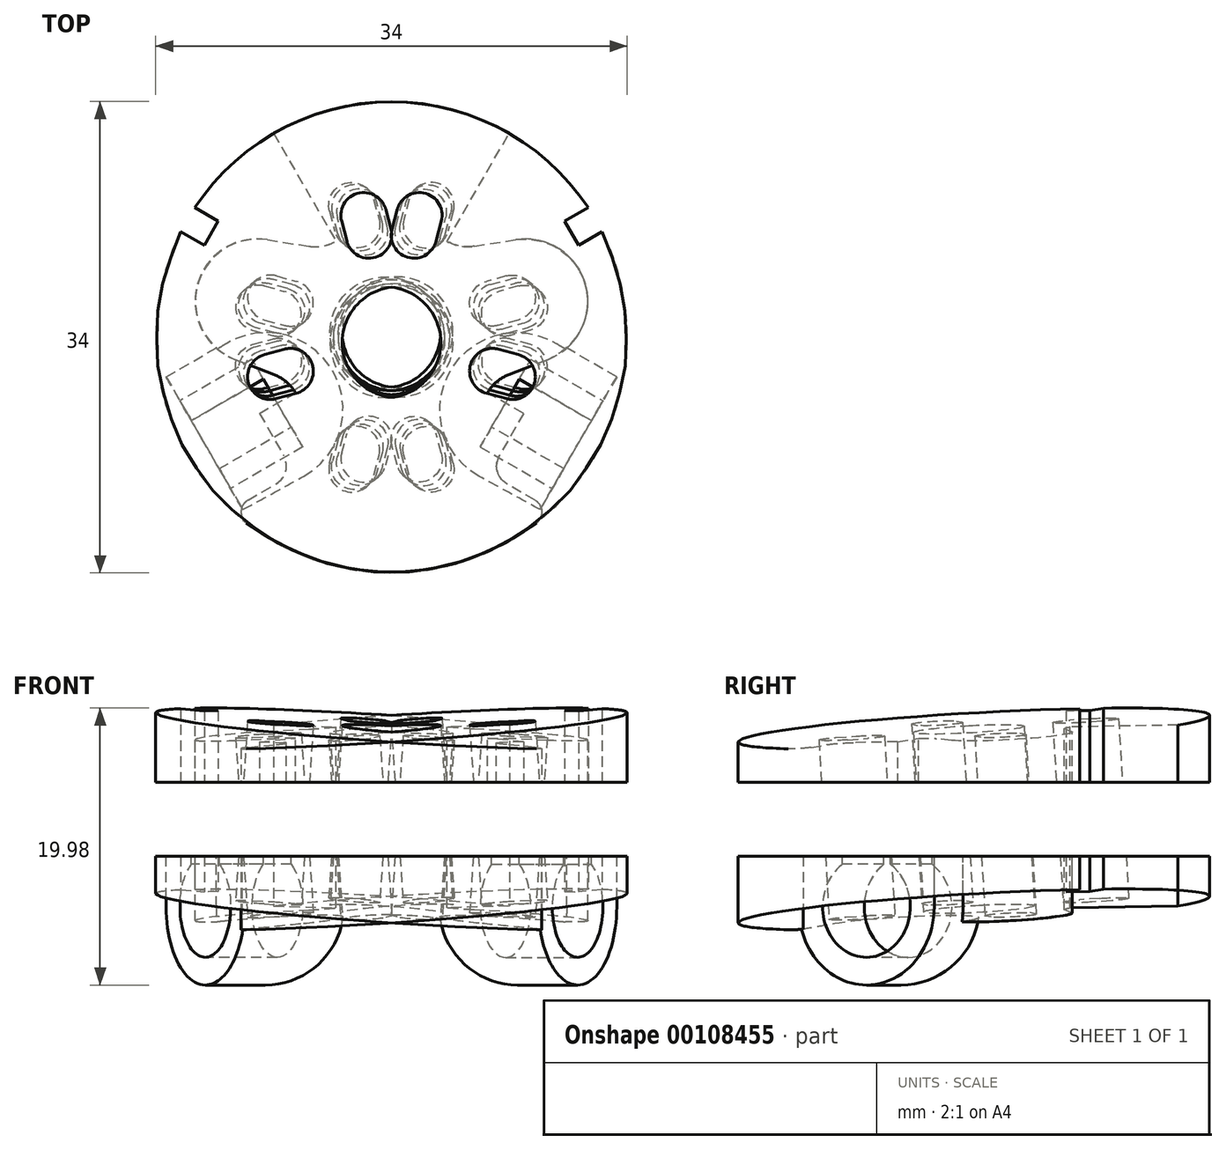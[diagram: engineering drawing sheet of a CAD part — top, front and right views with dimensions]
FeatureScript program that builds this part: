
annotation { "Feature Type Name" : "Feature", "Feature Type Description" : "" }
export const myFeature = defineFeature(function(context is Context, id is Id, definition is map)
    precondition{}
    {
        {
            var Q0;
            Q0=qCreatedBy(makeId("Top.planeOp"),FACE);
            var sketch = newSketch(context, id + "F0", { "sketchPlane" : qUnion([Q0])});
            skCircle(sketch, "E0", {"center": v(0, 0) * mm, "radius": 17 * mm});
            skLineSegment(sketch, "E1", {"start": v(10.93, 13.02) * mm, "end": v(-10.93, -13.02) * mm, "construction": true});
            skLineSegment(sketch, "E2", {"start": v(-8.5, -14.72) * mm, "end": v(8.5, 14.72) * mm, "construction": true});
            skSolve(sketch);
        }
        {
            var Q0;
            Q0=qCreatedBy(makeId("Top.planeOp"),FACE);
            var sketch = newSketch(context, id + "F1", { "sketchPlane" : qUnion([Q0])});
            skLineSegment(sketch, "E3", {"start": v(-8.5, -14.72) * mm, "end": v(8.5, 14.72) * mm, "construction": true});
            skPoint(sketch, "E4", {"position": v(0, 0) * mm});
            skLineSegment(sketch, "E5", {"start": v(0, 0) * mm, "end": v(9.18, 2.46) * mm, "construction": true});
            skPoint(sketch, "E6", {"position": v(7.73, 2.07) * mm});
            skArc(sketch, "E7", {"start": v(9.6, 0.91) * mm, "mid": v(10.72, 2.87) * mm, "end": v(8.76, 4) * mm, "construction": true});
            skArc(sketch, "E8", {"start": v(7.31, 3.62) * mm, "mid": v(6.18, 1.66) * mm, "end": v(8.14, 0.53) * mm, "construction": true});
            skLineSegment(sketch, "E9", {"start": v(8.76, 4) * mm, "end": v(7.31, 3.62) * mm, "construction": true});
            skLineSegment(sketch, "E10", {"start": v(9.6, 0.91) * mm, "end": v(8.14, 0.53) * mm, "construction": true});
            skLineSegment(sketch, "E11.1.0", {"start": v(-4, 8.76) * mm, "end": v(-3.62, 7.31) * mm, "construction": true});
            skLineSegment(sketch, "E11.1.1", {"start": v(-0.91, 9.6) * mm, "end": v(-0.53, 8.14) * mm, "construction": true});
            skArc(sketch, "E11.1.2", {"start": v(-3.62, 7.31) * mm, "mid": v(-1.66, 6.18) * mm, "end": v(-0.53, 8.14) * mm, "construction": true});
            skArc(sketch, "E11.1.3", {"start": v(-0.91, 9.6) * mm, "mid": v(-2.87, 10.72) * mm, "end": v(-4, 8.76) * mm, "construction": true});
            skPoint(sketch, "E11.1.4", {"position": v(-2.07, 7.73) * mm});
            skLineSegment(sketch, "E11.2.0", {"start": v(-8.76, -4) * mm, "end": v(-7.31, -3.62) * mm, "construction": true});
            skLineSegment(sketch, "E11.2.1", {"start": v(-9.6, -0.91) * mm, "end": v(-8.14, -0.53) * mm, "construction": true});
            skArc(sketch, "E11.2.2", {"start": v(-7.31, -3.62) * mm, "mid": v(-6.18, -1.66) * mm, "end": v(-8.14, -0.53) * mm, "construction": true});
            skArc(sketch, "E11.2.3", {"start": v(-9.6, -0.91) * mm, "mid": v(-10.72, -2.87) * mm, "end": v(-8.76, -4) * mm, "construction": true});
            skPoint(sketch, "E11.2.4", {"position": v(-7.73, -2.07) * mm});
            skLineSegment(sketch, "E11.3.0", {"start": v(4, -8.76) * mm, "end": v(3.62, -7.31) * mm, "construction": true});
            skLineSegment(sketch, "E11.3.1", {"start": v(0.91, -9.6) * mm, "end": v(0.53, -8.14) * mm, "construction": true});
            skArc(sketch, "E11.3.2", {"start": v(3.62, -7.31) * mm, "mid": v(1.66, -6.18) * mm, "end": v(0.53, -8.14) * mm, "construction": true});
            skArc(sketch, "E11.3.3", {"start": v(0.91, -9.6) * mm, "mid": v(2.87, -10.72) * mm, "end": v(4, -8.76) * mm, "construction": true});
            skPoint(sketch, "E11.3.4", {"position": v(2.07, -7.73) * mm});
            skSolve(sketch);
        }
        {
            var Q0;
            Q0=sQuery(id+"F0.wireOp",EDGE,"E1");
            cPlane(context, id + "F2", {"entities" : qUnion([Q0]), "cplaneType" : CPlaneType.LINE_ANGLE, "offset" : 25 * mm, "angle" : 355 * degree, "width" : 150 * mm, "height" : 150 * mm});
        }
        {
            var Q0;
            Q0=qCreatedBy(id+"F2.planeOp",FACE);
            var sketch = newSketch(context, id + "F3", { "sketchPlane" : qUnion([Q0])});
            skLineSegment(sketch, "E12", {"start": v(0, 0) * mm, "end": v(9.18, -2.44) * mm, "construction": true});
            skPoint(sketch, "E13", {"position": v(7.73, -2.06) * mm});
            skArc(sketch, "E14", {"start": v(8.76, -4.04) * mm, "mid": v(10.78, -2.87) * mm, "end": v(9.6, -0.85) * mm});
            skArc(sketch, "E15", {"start": v(8.16, -0.46) * mm, "mid": v(6.14, -1.63) * mm, "end": v(7.3, -3.65) * mm});
            skLineSegment(sketch, "E16", {"start": v(7.3, -3.65) * mm, "end": v(8.76, -4.04) * mm});
            skLineSegment(sketch, "E17", {"start": v(8.16, -0.46) * mm, "end": v(9.6, -0.85) * mm});
            skCircle(sketch, "E18", {"center": v(0, 0) * mm, "radius": 4 * mm});
            skLineSegment(sketch, "E19.1.0", {"start": v(0.46, 8.16) * mm, "end": v(0.85, 9.6) * mm});
            skLineSegment(sketch, "E19.1.1", {"start": v(3.65, 7.31) * mm, "end": v(4.04, 8.76) * mm});
            skArc(sketch, "E19.1.2", {"start": v(0.46, 8.16) * mm, "mid": v(1.63, 6.14) * mm, "end": v(3.65, 7.31) * mm});
            skArc(sketch, "E19.1.3", {"start": v(4.04, 8.76) * mm, "mid": v(2.87, 10.78) * mm, "end": v(0.85, 9.6) * mm});
            skPoint(sketch, "E19.1.4", {"position": v(2.06, 7.73) * mm});
            skLineSegment(sketch, "E19.2.0", {"start": v(-8.16, 0.47) * mm, "end": v(-9.6, 0.85) * mm});
            skLineSegment(sketch, "E19.2.1", {"start": v(-7.3, 3.66) * mm, "end": v(-8.76, 4.04) * mm});
            skArc(sketch, "E19.2.2", {"start": v(-8.16, 0.47) * mm, "mid": v(-6.14, 1.64) * mm, "end": v(-7.3, 3.66) * mm});
            skArc(sketch, "E19.2.3", {"start": v(-8.76, 4.04) * mm, "mid": v(-10.78, 2.87) * mm, "end": v(-9.6, 0.85) * mm});
            skPoint(sketch, "E19.2.4", {"position": v(-7.73, 2.06) * mm});
            skLineSegment(sketch, "E19.3.0", {"start": v(-0.47, -8.15) * mm, "end": v(-0.85, -9.6) * mm});
            skLineSegment(sketch, "E19.3.1", {"start": v(-3.65, -7.3) * mm, "end": v(-4.04, -8.76) * mm});
            skArc(sketch, "E19.3.2", {"start": v(-0.47, -8.15) * mm, "mid": v(-1.64, -6.14) * mm, "end": v(-3.65, -7.3) * mm});
            skArc(sketch, "E19.3.3", {"start": v(-4.04, -8.76) * mm, "mid": v(-2.87, -10.77) * mm, "end": v(-0.85, -9.6) * mm});
            skPoint(sketch, "E19.3.4", {"position": v(-2.06, -7.73) * mm});
            skSolve(sketch);
        }
        {
            var Q0;
            Q0=qSketchRegion(id+"F0",true);
            extrude(context, id + "F4", {"entities" : qUnion([Q0]), "endBound" : BoundingType.SYMMETRIC, "depth" : 25 * mm});
        }
        {
            var Q0;
            Q0=qSketchRegion(id+"F3",true);
            extrude(context, id + "F5", {"entities" : qUnion([Q0]), "operationType" : NewBodyOperationType.REMOVE, "endBound" : BoundingType.THROUGH_ALL, "oppositeDirection" : true, "depth" : 25 * mm, "hasSecondDirection" : true, "secondDirectionBound" : SecondDirectionBoundingType.THROUGH_ALL, "secondDirectionOppositeDirection" : false, "secondDirectionDepth" : 25 * mm});
        }
        {
            var Q0;
            Q0=qCreatedBy(id+"F2.planeOp",FACE);
            cPlane(context, id + "F6", {"entities" : qUnion([Q0]), "cplaneType" : CPlaneType.OFFSET, "offset" : 6.5 * mm, "oppositeDirection" : true, "width" : 150 * mm, "height" : 150 * mm});
        }
        {
            var Q0;
            Q0=qCreatedBy(id+"F2.planeOp",FACE);
            cPlane(context, id + "F7", {"entities" : qUnion([Q0]), "cplaneType" : CPlaneType.OFFSET, "offset" : 6.5 * mm, "width" : 150 * mm, "height" : 150 * mm});
        }
        {
            var Q0;
            Q0=qCreatedBy(id+"F6.planeOp",FACE);
            var sketch = newSketch(context, id + "F8", { "sketchPlane" : qUnion([Q0])});
            skCircle(sketch, "E20", {"center": v(0, 0) * mm, "radius": 20 * mm});
            skSolve(sketch);
        }
        {
            var Q0;
            Q0=qSketchRegion(id+"F8",true);
            var Q1;
            Q1=makeQuery(id+"F4.opExtrude","CAP_FACE",FACE,{"disambiguationData":[OSD([sQuery(id+"F0.wireOp",EDGE,"E0")])],"isStart":false});
            extrude(context, id + "F9", {"entities" : qUnion([Q0]), "operationType" : NewBodyOperationType.REMOVE, "endBound" : BoundingType.UP_TO_SURFACE, "oppositeDirection" : true, "endBoundEntityFace" : qUnion([Q1]), "depth" : 25 * mm});
        }
        {
            var Q0;
            Q0=qCreatedBy(id+"F7.planeOp",FACE);
            var sketch = newSketch(context, id + "F10", { "sketchPlane" : qUnion([Q0])});
            skCircle(sketch, "E21", {"center": v(0, 0) * mm, "radius": 20 * mm});
            skSolve(sketch);
        }
        {
            var Q0;
            Q0=qSketchRegion(id+"F10",true);
            var Q1;
            Q1=makeQuery(id+"F4.opExtrude","CAP_FACE",FACE,{"disambiguationData":[OSD([sQuery(id+"F0.wireOp",EDGE,"E0")])],"isStart":true});
            extrude(context, id + "F11", {"entities" : qUnion([Q0]), "operationType" : NewBodyOperationType.REMOVE, "endBound" : BoundingType.UP_TO_SURFACE, "endBoundEntityFace" : qUnion([Q1]), "depth" : 25 * mm});
        }
        {
            var Q0;
            Q0=qCreatedBy(makeId("Front.planeOp"),FACE);
            var sketch = newSketch(context, id + "F12", { "sketchPlane" : qUnion([Q0])});
            skLineSegment(sketch, "E22.bottom", {"start": v(20, 2.67) * mm, "end": v(-20, 2.67) * mm});
            skLineSegment(sketch, "E22.top", {"start": v(20, -2.67) * mm, "end": v(-20, -2.67) * mm});
            skLineSegment(sketch, "E22.left", {"start": v(20, 2.67) * mm, "end": v(20, -2.67) * mm});
            skLineSegment(sketch, "E22.right", {"start": v(-20, 2.67) * mm, "end": v(-20, -2.67) * mm});
            skPoint(sketch, "E22.middle", {"position": v(0, 0) * mm});
            skSolve(sketch);
        }
        {
            var Q0;
            Q0=qSketchRegion(id+"F12",true);
            extrude(context, id + "F13", {"entities" : qUnion([Q0]), "operationType" : NewBodyOperationType.REMOVE, "endBound" : BoundingType.THROUGH_ALL, "oppositeDirection" : true, "depth" : 25 * mm, "hasSecondDirection" : true, "secondDirectionBound" : SecondDirectionBoundingType.THROUGH_ALL, "secondDirectionOppositeDirection" : false, "secondDirectionDepth" : 25 * mm});
        }
        {
            var Q0;
            Q0=sQuery(id+"F1.wireOp",EDGE,"E3");
            cPlane(context, id + "F14", {"entities" : qUnion([Q0]), "cplaneType" : CPlaneType.LINE_ANGLE, "offset" : 25 * mm, "angle" : 90 * degree, "width" : 150 * mm, "height" : 150 * mm});
        }
        {
            var Q0;
            Q0=qCreatedBy(id+"F14.planeOp",FACE);
            cPlane(context, id + "F15", {"entities" : qUnion([Q0]), "cplaneType" : CPlaneType.OFFSET, "offset" : 17 * mm, "width" : 150 * mm, "height" : 150 * mm});
        }
        {
            var Q0;
            Q0=qCreatedBy(id+"F14.planeOp",FACE);
            cPlane(context, id + "F16", {"entities" : qUnion([Q0]), "cplaneType" : CPlaneType.OFFSET, "offset" : 17 * mm, "oppositeDirection" : true, "width" : 150 * mm, "height" : 150 * mm});
        }
        {
            var Q0;
            Q0=qCreatedBy(id+"F15.planeOp",FACE);
            var sketch = newSketch(context, id + "F17", { "sketchPlane" : qUnion([Q0])});
            skLineSegment(sketch, "E23.bottom", {"start": v(1, 12.5) * mm, "end": v(-1, 12.5) * mm});
            skLineSegment(sketch, "E23.top", {"start": v(1, -12.5) * mm, "end": v(-1, -12.5) * mm});
            skLineSegment(sketch, "E23.left", {"start": v(1, 12.5) * mm, "end": v(1, -12.5) * mm});
            skLineSegment(sketch, "E23.right", {"start": v(-1, 12.5) * mm, "end": v(-1, -12.5) * mm});
            skPoint(sketch, "E23.middle", {"position": v(0, 0) * mm});
            skSolve(sketch);
        }
        {
            var Q0;
            Q0=qSketchRegion(id+"F17",true);
            extrude(context, id + "F18", {"entities" : qUnion([Q0]), "operationType" : NewBodyOperationType.REMOVE, "oppositeDirection" : true, "depth" : 2 * mm});
        }
        {
            var Q0;
            Q0=qCreatedBy(id+"F16.planeOp",FACE);
            var sketch = newSketch(context, id + "F19", { "sketchPlane" : qUnion([Q0])});
            skLineSegment(sketch, "E24.0", {"start": v(-1, 12.5) * mm, "end": v(-1, -12.5) * mm});
            skLineSegment(sketch, "E24.1", {"start": v(1, 12.5) * mm, "end": v(-1, 12.5) * mm});
            skLineSegment(sketch, "E24.2", {"start": v(1, 12.5) * mm, "end": v(1, -12.5) * mm});
            skLineSegment(sketch, "E24.3", {"start": v(1, -12.5) * mm, "end": v(-1, -12.5) * mm});
            skSolve(sketch);
        }
        {
            var Q0;
            Q0=qSketchRegion(id+"F19",true);
            extrude(context, id + "F20", {"entities" : qUnion([Q0]), "operationType" : NewBodyOperationType.REMOVE, "depth" : 2 * mm});
        }
        {
            var Q0;
            Q0=qCreatedBy(makeId("Top.planeOp"),FACE);
            var sketch = newSketch(context, id + "F21", { "sketchPlane" : qUnion([Q0])});
            skLineSegment(sketch, "E25", {"start": v(0, 0) * mm, "end": v(28.57, -16.5) * mm, "construction": true});
            skLineSegment(sketch, "E26.0", {"start": v(8.33, -10.58) * mm, "end": v(13.09, -13.33) * mm});
            skLineSegment(sketch, "E27.0", {"start": v(13.33, -1.92) * mm, "end": v(18.09, -4.67) * mm});
            skLineSegment(sketch, "E28", {"start": v(7.78, -8.53) * mm, "end": v(11.28, -2.47) * mm});
            skLineSegment(sketch, "E29", {"start": v(13.09, -13.33) * mm, "end": v(18.09, -4.67) * mm});
            skPoint(sketch, "E30.visualSharp", {"position": v(7.03, -9.83) * mm});
            skArc(sketch, "E30.filletArc", {"start": v(7.78, -8.53) * mm, "mid": v(7.63, -9.67) * mm, "end": v(8.33, -10.58) * mm});
            skPoint(sketch, "E31.visualSharp", {"position": v(12.03, -1.17) * mm});
            skArc(sketch, "E31.filletArc", {"start": v(13.33, -1.92) * mm, "mid": v(12.19, -1.77) * mm, "end": v(11.28, -2.47) * mm});
            skSolve(sketch);
        }
        {
            var Q0;
            Q0=qSketchRegion(id+"F21",true);
            extrude(context, id + "F22", {"entities" : qUnion([Q0]), "operationType" : NewBodyOperationType.REMOVE, "endBound" : BoundingType.THROUGH_ALL, "oppositeDirection" : true, "depth" : 25 * mm, "hasSecondDirection" : true, "secondDirectionBound" : SecondDirectionBoundingType.THROUGH_ALL, "secondDirectionOppositeDirection" : false, "secondDirectionDepth" : 25 * mm});
        }
        {
            var Q0;
            {var subQ0=makeQuery(id+"F9.boolean.opBoolean","COPY",FACE,{"derivedFrom":makeQuery(id+"F9.opExtrude","CAP_FACE",FACE,{"disambiguationData":[OSD([sQuery(id+"F8.wireOp",EDGE,"E20")])],"isStart":true})});Q0=makeQuery(id+"F22.boolean.opBoolean","INTERSECT",EDGE,{"derivedFrom":[makeQuery(id+"F20.boolean.opBoolean","SPLIT",FACE,{"disambiguationData":[TD([makeQuery(id+"F18.boolean.opBoolean","COPY",FACE,{"disambiguationData":[OD(0.0)],"derivedFrom":makeQuery(id+"F18.opExtrude","SWEPT_FACE",FACE,{"disambiguationData":[OSD([sQuery(id+"F17.wireOp",EDGE,"E23.right")])]})})])],"derivedFrom":makeQuery(id+"F13.boolean.opBoolean","SPLIT",FACE,{"disambiguationData":[TD([subQ0])],"derivedFrom":makeQuery(id+"F4.opExtrude","SWEPT_FACE",FACE,{"disambiguationData":[OSD([sQuery(id+"F0.wireOp",EDGE,"E0")])]})})}),makeQuery(id+"F22.opExtrude","SWEPT_FACE",FACE,{"disambiguationData":[OSD([sQuery(id+"F21.wireOp",EDGE,"E26.0")])]})]});}
            var Q1;
            {var subQ0=makeQuery(id+"F9.boolean.opBoolean","COPY",FACE,{"derivedFrom":makeQuery(id+"F9.opExtrude","CAP_FACE",FACE,{"disambiguationData":[OSD([sQuery(id+"F8.wireOp",EDGE,"E20")])],"isStart":true})});Q1=makeQuery(id+"F22.boolean.opBoolean","INTERSECT",EDGE,{"derivedFrom":[makeQuery(id+"F20.boolean.opBoolean","SPLIT",FACE,{"disambiguationData":[TD([makeQuery(id+"F18.boolean.opBoolean","COPY",FACE,{"disambiguationData":[OD(0.0)],"derivedFrom":makeQuery(id+"F18.opExtrude","SWEPT_FACE",FACE,{"disambiguationData":[OSD([sQuery(id+"F17.wireOp",EDGE,"E23.left")])]})})])],"derivedFrom":makeQuery(id+"F13.boolean.opBoolean","SPLIT",FACE,{"disambiguationData":[TD([subQ0])],"derivedFrom":makeQuery(id+"F4.opExtrude","SWEPT_FACE",FACE,{"disambiguationData":[OSD([sQuery(id+"F0.wireOp",EDGE,"E0")])]})})}),makeQuery(id+"F22.opExtrude","SWEPT_FACE",FACE,{"disambiguationData":[OSD([sQuery(id+"F21.wireOp",EDGE,"E27.0")])]})]});}
            var Q2;
            {var subQ0=makeQuery(id+"F11.boolean.opBoolean","COPY",FACE,{"derivedFrom":makeQuery(id+"F11.opExtrude","CAP_FACE",FACE,{"disambiguationData":[OSD([sQuery(id+"F10.wireOp",EDGE,"E21")])],"isStart":true})});Q2=makeQuery(id+"F22.boolean.opBoolean","INTERSECT",EDGE,{"derivedFrom":[makeQuery(id+"F20.boolean.opBoolean","SPLIT",FACE,{"disambiguationData":[TD([makeQuery(id+"F18.boolean.opBoolean","COPY",FACE,{"disambiguationData":[OD(1.0)],"derivedFrom":makeQuery(id+"F18.opExtrude","SWEPT_FACE",FACE,{"disambiguationData":[OSD([sQuery(id+"F17.wireOp",EDGE,"E23.right")])]})})])],"derivedFrom":makeQuery(id+"F13.boolean.opBoolean","SPLIT",FACE,{"disambiguationData":[TD([subQ0])],"derivedFrom":makeQuery(id+"F4.opExtrude","SWEPT_FACE",FACE,{"disambiguationData":[OSD([sQuery(id+"F0.wireOp",EDGE,"E0")])]})})}),makeQuery(id+"F22.opExtrude","SWEPT_FACE",FACE,{"disambiguationData":[OSD([sQuery(id+"F21.wireOp",EDGE,"E26.0")])]})]});}
            var Q3;
            {var subQ0=makeQuery(id+"F11.boolean.opBoolean","COPY",FACE,{"derivedFrom":makeQuery(id+"F11.opExtrude","CAP_FACE",FACE,{"disambiguationData":[OSD([sQuery(id+"F10.wireOp",EDGE,"E21")])],"isStart":true})});Q3=makeQuery(id+"F22.boolean.opBoolean","INTERSECT",EDGE,{"derivedFrom":[makeQuery(id+"F20.boolean.opBoolean","SPLIT",FACE,{"disambiguationData":[TD([makeQuery(id+"F18.boolean.opBoolean","COPY",FACE,{"disambiguationData":[OD(1.0)],"derivedFrom":makeQuery(id+"F18.opExtrude","SWEPT_FACE",FACE,{"disambiguationData":[OSD([sQuery(id+"F17.wireOp",EDGE,"E23.left")])]})})])],"derivedFrom":makeQuery(id+"F13.boolean.opBoolean","SPLIT",FACE,{"disambiguationData":[TD([subQ0])],"derivedFrom":makeQuery(id+"F4.opExtrude","SWEPT_FACE",FACE,{"disambiguationData":[OSD([sQuery(id+"F0.wireOp",EDGE,"E0")])]})})}),makeQuery(id+"F22.opExtrude","SWEPT_FACE",FACE,{"disambiguationData":[OSD([sQuery(id+"F21.wireOp",EDGE,"E27.0")])]})]});}
            fillet(context, id + "F23", {"entities" : qUnion([Q0, Q1, Q2, Q3]), "radius" : 1 * mm, "tangentPropagation" : true, "allowEdgeOverflow" : false});
        }
        {
            var Q0;
            Q0=qCreatedBy(makeId("Top.planeOp"),FACE);
            var sketch = newSketch(context, id + "F24", { "sketchPlane" : qUnion([Q0])});
            skLineSegment(sketch, "E32", {"start": v(0, 0) * mm, "end": v(9.53, -5.5) * mm, "construction": true});
            skLineSegment(sketch, "E33", {"start": v(0, 0) * mm, "end": v(5.5, 9.53) * mm, "construction": true});
            skArc(sketch, "E34.0", {"start": v(16.45, -9.5) * mm, "mid": v(18.35, 4.92) * mm, "end": v(9.5, 16.45) * mm});
            skArc(sketch, "E35", {"start": v(4, 6.93) * mm, "mid": v(4.95, 6.58) * mm, "end": v(5.97, 6.56) * mm});
            skArc(sketch, "E36", {"start": v(8.45, -2.7) * mm, "mid": v(7.58, -3.22) * mm, "end": v(6.93, -4) * mm});
            skLineSegment(sketch, "E37", {"start": v(0, 0) * mm, "end": v(9.66, 2.59) * mm, "construction": true});
            skArc(sketch, "E38", {"start": v(11.28, -1.61) * mm, "mid": v(14, 3.75) * mm, "end": v(8.96, 7.03) * mm});
            skLineSegment(sketch, "E39", {"start": v(5.97, 6.56) * mm, "end": v(8.96, 7.03) * mm});
            skLineSegment(sketch, "E40", {"start": v(8.45, -2.7) * mm, "end": v(11.28, -1.61) * mm});
            skLineSegment(sketch, "E41", {"start": v(6.93, -4) * mm, "end": v(16.45, -9.5) * mm});
            skLineSegment(sketch, "E42", {"start": v(4, 6.93) * mm, "end": v(9.5, 16.45) * mm});
            skSolve(sketch);
        }
        {
            var Q0;
            Q0=qSketchRegion(id+"F24",true);
            extrude(context, id + "F25", {"entities" : qUnion([Q0]), "operationType" : NewBodyOperationType.REMOVE, "endBound" : BoundingType.THROUGH_ALL, "oppositeDirection" : true, "depth" : 25 * mm, "hasSecondDirection" : true, "secondDirectionBound" : SecondDirectionBoundingType.THROUGH_ALL, "secondDirectionOppositeDirection" : false, "secondDirectionDepth" : 25 * mm});
        }
        {
            var Q0;
            Q0=qCreatedBy(makeId("Front.planeOp"),FACE);
            var sketch = newSketch(context, id + "F26", { "sketchPlane" : qUnion([Q0])});
            skLineSegment(sketch, "E43", {"start": v(0, 0) * mm, "end": v(0, 59.66) * mm, "construction": true});
            skSolve(sketch);
        }
        {
            var Q0;
            Q0=sQuery(id+"F0.wireOp",EDGE,"E2");
            cPlane(context, id + "F27", {"entities" : qUnion([Q0]), "cplaneType" : CPlaneType.LINE_ANGLE, "offset" : 25 * mm, "angle" : 90 * degree, "width" : 150 * mm, "height" : 150 * mm});
        }
        {
            var Q0;
            Q0=qCreatedBy(id+"F27.planeOp",FACE);
            cPlane(context, id + "F28", {"entities" : qUnion([Q0]), "cplaneType" : CPlaneType.OFFSET, "offset" : 10.5 * mm, "width" : 150 * mm, "height" : 150 * mm});
        }
        {
            var Q0;
            Q0=qCreatedBy(id+"F28.planeOp",FACE);
            var sketch = newSketch(context, id + "F29", { "sketchPlane" : qUnion([Q0])});
            skLineSegment(sketch, "E44", {"start": v(0, 0) * mm, "end": v(0, -6.32) * mm, "construction": true});
            skCircle(sketch, "E45", {"center": v(0, -6.32) * mm, "radius": 3.65 * mm, "construction": true});
            skArc(sketch, "E46.0", {"start": v(-5.65, -6.32) * mm, "mid": v(0, -11.97) * mm, "end": v(5.65, -6.32) * mm});
            skLineSegment(sketch, "E47", {"start": v(-5.65, -6.32) * mm, "end": v(-5.65, -2.67) * mm});
            skLineSegment(sketch, "E48", {"start": v(5.65, -6.32) * mm, "end": v(5.65, -2.67) * mm});
            skLineSegment(sketch, "E49", {"start": v(5.65, -2.67) * mm, "end": v(-5.65, -2.67) * mm});
            skSolve(sketch);
        }
        {
            var Q0;
            Q0 = qSketchRegion(id + "F29", true);
            extrude(context, id + "F30", {"entities" : qUnion([Q0]), "operationType" : NewBodyOperationType.ADD, "depth" : 5 * mm});
        }
        {
            var Q0;
            Q0=makeQuery(id+"F30.boolean.opBoolean","MERGE",FACE,{"derivedFrom":[makeQuery(id+"F13.boolean.opBoolean","COPY",FACE,{"derivedFrom":makeQuery(id+"F13.opExtrude","SWEPT_FACE",FACE,{"disambiguationData":[OSD([sQuery(id+"F12.wireOp",EDGE,"E22.top")])]})}),makeQuery(id+"F30.opExtrude","SWEPT_FACE",FACE,{"disambiguationData":[OSD([sQuery(id+"F29.wireOp",EDGE,"E49")])]})]});
            var sketch = newSketch(context, id + "F31", { "sketchPlane" : qUnion([Q0])});
            skLineSegment(sketch, "E50.0", {"start": v(6.56, -5.97) * mm, "end": v(7.02, -8.85) * mm});
            skLineSegment(sketch, "E51.0", {"start": v(11.17, -1.65) * mm, "end": v(7.02, -8.85) * mm});
            skLineSegment(sketch, "E52.0", {"start": v(8.45, -2.7) * mm, "end": v(11.17, -1.65) * mm});
            skArc(sketch, "E53.0", {"start": v(8.45, -2.7) * mm, "mid": v(6.93, -4) * mm, "end": v(6.56, -5.97) * mm});
            skSolve(sketch);
        }
        {
            var Q0;
            Q0 = qSketchRegion(id + "F31", true);
            var Q1;
            Q1=makeQuery(id+"F11.boolean.opBoolean","COPY",FACE,{"derivedFrom":makeQuery(id+"F11.opExtrude","CAP_FACE",FACE,{"disambiguationData":[OSD([sQuery(id+"F10.wireOp",EDGE,"E21")])],"isStart":true})});
            extrude(context, id + "F32", {"entities" : qUnion([Q0]), "operationType" : NewBodyOperationType.ADD, "endBound" : BoundingType.UP_TO_SURFACE, "oppositeDirection" : true, "endBoundEntityFace" : qUnion([Q1]), "depth" : 25 * mm});
        }
        {
            var Q0;
            Q0=qCreatedBy(id+"F28.planeOp",FACE);
            var sketch = newSketch(context, id + "F33", { "sketchPlane" : qUnion([Q0])});
            skArc(sketch, "E54.0", {"start": v(-5.65, -6.32) * mm, "mid": v(0, -11.97) * mm, "end": v(5.65, -6.32) * mm});
            skLineSegment(sketch, "E55", {"start": v(-5.65, -6.32) * mm, "end": v(5.65, -6.32) * mm});
            skSolve(sketch);
        }
        {
            var Q0;
            Q0 = qSketchRegion(id + "F33", true);
            var Q1;
            Q1=sQuery(id+"F33.wireOp",EDGE,"E55");
            revolve(context, id + "F34", {"operationType" : NewBodyOperationType.ADD, "entities" : qUnion([Q0]), "axis" : qUnion([Q1]), "revolveType" : RevolveType.ONE_DIRECTION, "angle" : 90 * degree});
        }
        {
            var Q0;
            Q0=makeQuery(id+"F30.opExtrude","CAP_FACE",FACE,{"disambiguationData":[OSD([sQuery(id+"F29.wireOp",EDGE,"E46.0"),sQuery(id+"F29.wireOp",EDGE,"E47"),sQuery(id+"F29.wireOp",EDGE,"E48"),sQuery(id+"F29.wireOp",EDGE,"E49")])],"isStart":false});
            var sketch = newSketch(context, id + "F35", { "sketchPlane" : qUnion([Q0])});
            skArc(sketch, "E56.0", {"start": v(-2, -3.26) * mm, "mid": v(0, -9.97) * mm, "end": v(2, -3.26) * mm});
            skLineSegment(sketch, "E57", {"start": v(-2, -3.26) * mm, "end": v(-2, -1.67) * mm});
            skLineSegment(sketch, "E58", {"start": v(2, -3.26) * mm, "end": v(2, -1.67) * mm});
            skLineSegment(sketch, "E59", {"start": v(2, -1.67) * mm, "end": v(-2, -1.67) * mm});
            skPoint(sketch, "E60", {"position": v(0, -1.67) * mm});
            skSolve(sketch);
        }
        {
            var Q0;
            Q0 = qSketchRegion(id + "F35", true);
            extrude(context, id + "F36", {"entities" : qUnion([Q0]), "operationType" : NewBodyOperationType.REMOVE, "oppositeDirection" : true, "depth" : 6 * mm});
        }
        {
            var Q0;
            Q0=makeQuery(id+"F13.boolean.opBoolean","SPLIT",BODY,{"disambiguationData":[OD(0.0)],"derivedFrom":makeQuery(id+"F4.opExtrude","SWEPT_BODY",BODY,{"disambiguationData":[OSD([sQuery(id+"F0.wireOp",EDGE,"E0")])]})});
            var Q1;
            Q1=makeQuery(id+"F13.boolean.opBoolean","SPLIT",BODY,{"disambiguationData":[OD(1.0)],"derivedFrom":makeQuery(id+"F4.opExtrude","SWEPT_BODY",BODY,{"disambiguationData":[OSD([sQuery(id+"F0.wireOp",EDGE,"E0")])]})});
            var Q2;
            Q2=qCreatedBy(makeId("Right.planeOp"),FACE);
            mirror(context, id + "F37", {"entities" : qUnion([Q0, Q1]), "mirrorPlane" : qUnion([Q2])});
        }
    });
